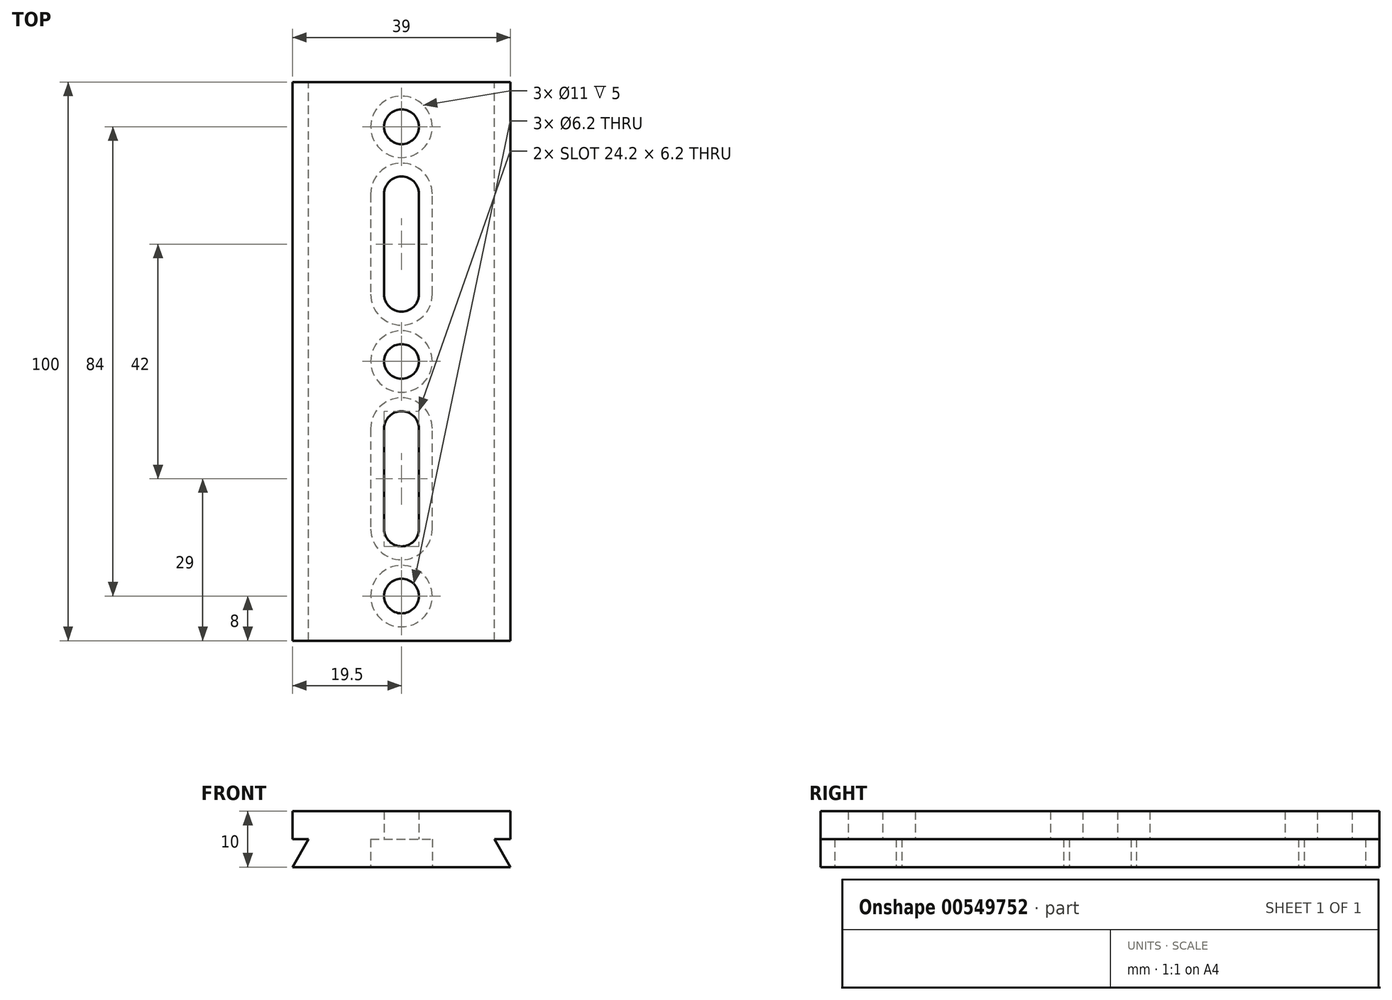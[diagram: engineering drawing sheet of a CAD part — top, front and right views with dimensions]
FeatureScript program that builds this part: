
annotation { "Feature Type Name" : "Feature", "Feature Type Description" : "" }
export const myFeature = defineFeature(function(context is Context, id is Id, definition is map)
    precondition{}
    {
        {
            var Q0;
            Q0=qCreatedBy(makeId("Front.planeOp"),FACE);
            var sketch = newSketch(context, id + "F0", { "sketchPlane" : qUnion([Q0])});
            skLineSegment(sketch, "E0.bottom", {"start": v(19.5, -2.5) * mm, "end": v(16.61, -2.5) * mm});
            skLineSegment(sketch, "E0.top", {"start": v(19.5, 2.5) * mm, "end": v(-19.5, 2.5) * mm});
            skLineSegment(sketch, "E0.left", {"start": v(19.5, -2.5) * mm, "end": v(19.5, 2.5) * mm});
            skLineSegment(sketch, "E0.right", {"start": v(-19.5, -2.5) * mm, "end": v(-19.5, 2.5) * mm});
            skPoint(sketch, "E0.middle", {"position": v(0, 0) * mm});
            skLineSegment(sketch, "E1", {"start": v(-16.61, -2.5) * mm, "end": v(-19.5, -7.5) * mm});
            skLineSegment(sketch, "E2", {"start": v(-19.5, -7.5) * mm, "end": v(19.5, -7.5) * mm});
            skLineSegment(sketch, "E3", {"start": v(19.5, -7.5) * mm, "end": v(16.61, -2.5) * mm});
            skPoint(sketch, "E4.endSnap0", {"position": v(0, 2.5) * mm});
            skLineSegment(sketch, "E5.trimOffspring", {"start": v(-16.61, -2.5) * mm, "end": v(-19.5, -2.5) * mm});
            skSolve(sketch);
        }
        {
            var Q0;
            Q0=makeQuery(id+"F0.imprint","IMPRINT",FACE,{"disambiguationData":[TD([[makeQuery(id+"F0.imprint","IMPRINT",EDGE,{"derivedFrom":sQuery(id+"F0.wireOp",EDGE,"E0.bottom")}),-1.0]])]});
            extrude(context, id + "F1", {"entities" : qUnion([Q0]), "endBound" : BoundingType.SYMMETRIC, "depth" : 100 * mm, "offsetDistance" : 25 * mm});
        }
        {
            var Q0;
            Q0=makeQuery(id+"F1.opExtrude","SWEPT_FACE",FACE,{"disambiguationData":[OSD([sQuery(id+"F0.wireOp",EDGE,"E2")])]});
            var sketch = newSketch(context, id + "F2", { "sketchPlane" : qUnion([Q0])});
            skCircle(sketch, "E6", {"center": v(0, 0) * mm, "radius": 5.5 * mm});
            skCircle(sketch, "E7", {"center": v(0, -42) * mm, "radius": 5.5 * mm});
            skCircle(sketch, "E8", {"center": v(0, 42) * mm, "radius": 5.5 * mm});
            skCircle(sketch, "E9", {"center": v(0, -30) * mm, "radius": 5.5 * mm});
            skCircle(sketch, "E10", {"center": v(0, -12) * mm, "radius": 5.5 * mm});
            skLineSegment(sketch, "E11", {"start": v(-5.5, -30) * mm, "end": v(-5.5, -12) * mm});
            skLineSegment(sketch, "E12", {"start": v(5.5, -12) * mm, "end": v(5.5, -30) * mm});
            skCircle(sketch, "E13", {"center": v(0, 12) * mm, "radius": 5.5 * mm});
            skCircle(sketch, "E14", {"center": v(0, 30) * mm, "radius": 5.5 * mm});
            skLineSegment(sketch, "E15", {"start": v(-5.5, 12) * mm, "end": v(-5.5, 30) * mm});
            skLineSegment(sketch, "E16", {"start": v(5.5, 30) * mm, "end": v(5.5, 12) * mm});
            skSolve(sketch);
        }
        {
            var Q0;
            Q0 = qSketchRegion(id + "F2", true);
            extrude(context, id + "F3", {"entities" : qUnion([Q0]), "operationType" : NewBodyOperationType.REMOVE, "oppositeDirection" : true, "depth" : 5 * mm, "offsetDistance" : 25 * mm});
        }
        {
            var Q0;
            Q0=makeQuery(id+"F3.boolean.opBoolean","COPY",FACE,{"derivedFrom":makeQuery(id+"F3.opExtrude","CAP_FACE",FACE,{"disambiguationData":[OSD([sQuery(id+"F2.wireOp",EDGE,"E7")])],"isStart":false})});
            var sketch = newSketch(context, id + "F4", { "sketchPlane" : qUnion([Q0])});
            skCircle(sketch, "E17", {"center": v(0, -42) * mm, "radius": 3.1 * mm});
            skCircle(sketch, "E18", {"center": v(0, 0) * mm, "radius": 3.1 * mm});
            skCircle(sketch, "E19", {"center": v(0, 42) * mm, "radius": 3.1 * mm});
            skCircle(sketch, "E20", {"center": v(0, -30) * mm, "radius": 3.1 * mm});
            skCircle(sketch, "E21", {"center": v(0, -12) * mm, "radius": 3.1 * mm});
            skCircle(sketch, "E22", {"center": v(0, 12) * mm, "radius": 3.1 * mm});
            skCircle(sketch, "E23", {"center": v(0, 30) * mm, "radius": 3.1 * mm});
            skLineSegment(sketch, "E24", {"start": v(-3.1, -30) * mm, "end": v(-3.1, -12) * mm});
            skLineSegment(sketch, "E25", {"start": v(3.1, -12) * mm, "end": v(3.1, -30) * mm});
            skLineSegment(sketch, "E26", {"start": v(-3.1, 12) * mm, "end": v(-3.1, 30) * mm});
            skLineSegment(sketch, "E27", {"start": v(3.1, 12) * mm, "end": v(3.1, 30) * mm});
            skSolve(sketch);
        }
        {
            var Q0;
            Q0 = qSketchRegion(id + "F4", true);
            extrude(context, id + "F5", {"entities" : qUnion([Q0]), "operationType" : NewBodyOperationType.REMOVE, "endBound" : BoundingType.THROUGH_ALL, "oppositeDirection" : true, "depth" : 25 * mm, "offsetDistance" : 25 * mm});
        }
    });
